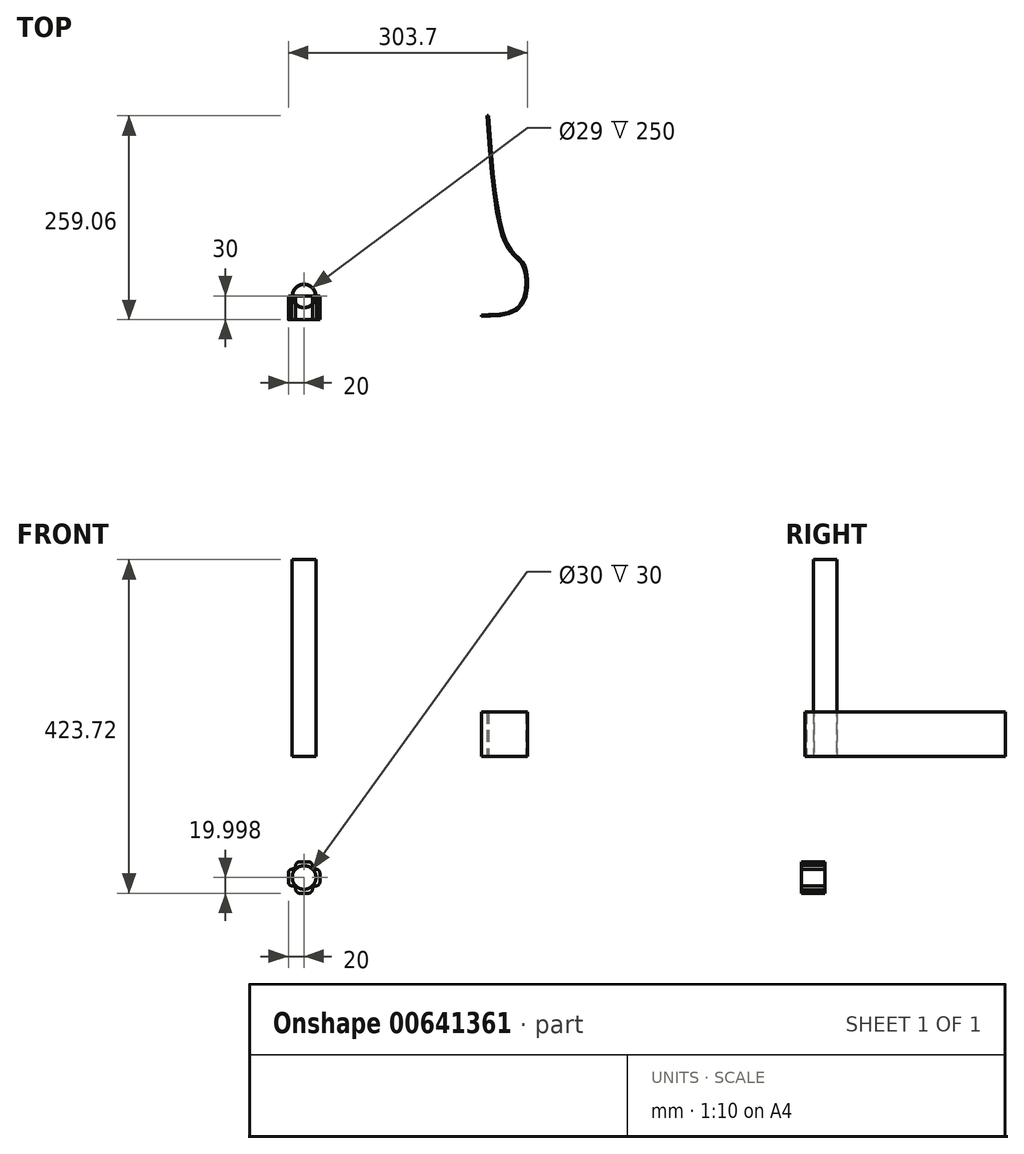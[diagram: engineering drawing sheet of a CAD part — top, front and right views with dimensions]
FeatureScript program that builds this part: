
annotation { "Feature Type Name" : "Feature", "Feature Type Description" : "" }
export const myFeature = defineFeature(function(context is Context, id is Id, definition is map)
    precondition{}
    {
        {
            var Q0;
            Q0=qCreatedBy(makeId("Top.planeOp"),FACE);
            var sketch = newSketch(context, id + "F0", { "sketchPlane" : qUnion([Q0])});
            skCircle(sketch, "E0", {"center": v(0, 0) * mm, "radius": 15 * mm});
            skCircle(sketch, "E1", {"center": v(0, 0) * mm, "radius": 14.5 * mm});
            skSolve(sketch);
        }
        {
            var Q0;
            Q0=qSketchRegion(id+"F0",true);
            extrude(context, id + "F1", {"entities" : qUnion([Q0]), "depth" : 250 * mm});
        }
        {
            var Q0;
            Q0=qCreatedBy(makeId("Front.planeOp"),FACE);
            var sketch = newSketch(context, id + "F2", { "sketchPlane" : qUnion([Q0])});
            skCircle(sketch, "E2", {"center": v(0, -153.72) * mm, "radius": 15 * mm});
            skLineSegment(sketch, "E3.0", {"start": v(-5.6, -133.72) * mm, "end": v(5.6, -133.72) * mm});
            skLineSegment(sketch, "E3.1", {"start": v(20, -148.12) * mm, "end": v(20, -159.33) * mm});
            skLineSegment(sketch, "E3.2", {"start": v(5.6, -173.72) * mm, "end": v(-5.6, -173.72) * mm});
            skLineSegment(sketch, "E3.3", {"start": v(-20, -159.33) * mm, "end": v(-20, -148.12) * mm});
            skPoint(sketch, "E3.0.midPoint", {"position": v(0, -133.72) * mm});
            skPoint(sketch, "E4", {"position": v(20, -153.72) * mm});
            skLineSegment(sketch, "E5", {"start": v(20, -133.72) * mm, "end": v(-20, -173.72) * mm, "construction": true});
            skLineSegment(sketch, "E6", {"start": v(20, -173.72) * mm, "end": v(-20, -133.72) * mm, "construction": true});
            skPoint(sketch, "E7", {"position": v(10.6, -143.12) * mm});
            skPoint(sketch, "E8", {"position": v(-10.6, -164.33) * mm});
            skPoint(sketch, "E9", {"position": v(10.6, -164.33) * mm});
            skPoint(sketch, "E10", {"position": v(-10.6, -143.12) * mm});
            skLineSegment(sketch, "E11.top", {"start": v(15.6, -143.12) * mm, "end": v(15, -143.12) * mm});
            skLineSegment(sketch, "E11.right", {"start": v(10.6, -138.12) * mm, "end": v(10.6, -138.72) * mm});
            skLineSegment(sketch, "E12.top", {"start": v(15.6, -164.33) * mm, "end": v(15, -164.33) * mm});
            skLineSegment(sketch, "E12.right", {"start": v(10.6, -169.33) * mm, "end": v(10.6, -168.72) * mm});
            skLineSegment(sketch, "E13.top", {"start": v(-15.6, -164.33) * mm, "end": v(-15, -164.33) * mm});
            skLineSegment(sketch, "E13.right", {"start": v(-10.6, -169.33) * mm, "end": v(-10.6, -168.72) * mm});
            skLineSegment(sketch, "E14.top", {"start": v(-15.6, -143.12) * mm, "end": v(-15, -143.12) * mm});
            skLineSegment(sketch, "E14.right", {"start": v(-10.6, -138.12) * mm, "end": v(-10.6, -138.72) * mm});
            skArc(sketch, "E15.filletArc", {"start": v(-10.6, -169.33) * mm, "mid": v(-12.07, -165.8) * mm, "end": v(-15.6, -164.33) * mm});
            skArc(sketch, "E16.filletArc", {"start": v(-15.6, -143.12) * mm, "mid": v(-12.07, -141.65) * mm, "end": v(-10.6, -138.12) * mm});
            skArc(sketch, "E17.filletArc", {"start": v(10.6, -138.12) * mm, "mid": v(12.07, -141.65) * mm, "end": v(15.6, -143.12) * mm});
            skArc(sketch, "E18.filletArc", {"start": v(15.6, -164.33) * mm, "mid": v(12.07, -165.8) * mm, "end": v(10.6, -169.33) * mm});
            skPoint(sketch, "E19.visualSharp", {"position": v(20, -164.33) * mm});
            skArc(sketch, "E19.filletArc", {"start": v(15, -164.33) * mm, "mid": v(18.54, -162.86) * mm, "end": v(20, -159.33) * mm});
            skPoint(sketch, "E20.visualSharp", {"position": v(20, -143.12) * mm});
            skArc(sketch, "E20.filletArc", {"start": v(20, -148.12) * mm, "mid": v(18.54, -144.58) * mm, "end": v(15, -143.12) * mm});
            skPoint(sketch, "E21.visualSharp", {"position": v(10.6, -133.72) * mm});
            skArc(sketch, "E21.filletArc", {"start": v(10.6, -138.72) * mm, "mid": v(9.14, -135.19) * mm, "end": v(5.6, -133.72) * mm});
            skPoint(sketch, "E22.visualSharp", {"position": v(-10.6, -133.72) * mm});
            skArc(sketch, "E22.filletArc", {"start": v(-5.6, -133.72) * mm, "mid": v(-9.14, -135.19) * mm, "end": v(-10.6, -138.72) * mm});
            skPoint(sketch, "E23.visualSharp", {"position": v(-20, -143.12) * mm});
            skArc(sketch, "E23.filletArc", {"start": v(-15, -143.12) * mm, "mid": v(-18.54, -144.58) * mm, "end": v(-20, -148.12) * mm});
            skPoint(sketch, "E24.visualSharp", {"position": v(-20, -164.33) * mm});
            skArc(sketch, "E24.filletArc", {"start": v(-20, -159.33) * mm, "mid": v(-18.54, -162.86) * mm, "end": v(-15, -164.33) * mm});
            skPoint(sketch, "E25.visualSharp", {"position": v(-10.6, -173.72) * mm});
            skArc(sketch, "E25.filletArc", {"start": v(-10.6, -168.72) * mm, "mid": v(-9.14, -172.26) * mm, "end": v(-5.6, -173.72) * mm});
            skPoint(sketch, "E26.visualSharp", {"position": v(10.6, -173.72) * mm});
            skArc(sketch, "E26.filletArc", {"start": v(5.6, -173.72) * mm, "mid": v(9.14, -172.26) * mm, "end": v(10.6, -168.72) * mm});
            skSolve(sketch);
        }
        {
            var Q0;
            Q0=qSketchRegion(id+"F2",true);
            extrude(context, id + "F3", {"entities" : qUnion([Q0]), "depth" : 30 * mm});
        }
        {
            var Q0;
            Q0=qCreatedBy(makeId("Top.planeOp"),FACE);
            var sketch = newSketch(context, id + "F4", { "sketchPlane" : qUnion([Q0])});
            skLineSegment(sketch, "E27", {"start": v(195.56, 229.06) * mm, "end": v(195.56, -25.94) * mm, "construction": true});
            skLineSegment(sketch, "E28", {"start": v(225.56, 229.06) * mm, "end": v(225.56, -25.94) * mm});
            skFitSpline(sketch, "E29", {"points": [v(234.4, 229.06) * mm, v(258.34, 65.82) * mm, v(275.52, 45.77) * mm, v(282.68, 29.07) * mm, v(274.56, -14.36) * mm, v(225.56, -25.94) * mm, v(195.56, -25.94) * mm], "startDerivative": vector(48.25, -659.53) * mm, "endDerivative": vector(-199.67, 0.53) * mm});
            skFitSpline(sketch, "E30.0", {"points": [v(232.41, 228.92) * mm, v(233.42, 215.18) * mm, v(235.43, 187.69) * mm, v(238.89, 148.44) * mm, v(242.52, 119.07) * mm, v(246.1, 98.57) * mm, v(248.66, 87.2) * mm, v(250.95, 79.09) * mm, v(252.8, 73.53) * mm, v(254.45, 69.35) * mm, v(255.85, 66.29) * mm, v(257.3, 63.42) * mm, v(259.22, 60.23) * mm, v(262.4, 55.84) * mm, v(265.63, 52.37) * mm, v(268.7, 49.5) * mm, v(270.85, 47.55) * mm, v(272.47, 46.05) * mm, v(273.63, 44.87) * mm, v(274.7, 43.7) * mm, v(275.9, 42.2) * mm, v(277.54, 39.67) * mm, v(278.84, 36.73) * mm, v(279.87, 33.11) * mm, v(280.42, 30.5) * mm, v(280.8, 28.19) * mm, v(281.14, 25.71) * mm, v(281.48, 22.38) * mm, v(281.71, 18.09) * mm, v(281.7, 12.12) * mm, v(281.16, 5.99) * mm, v(279.92, 0.12) * mm, v(278.6, -4.05) * mm, v(276.87, -7.88) * mm, v(275.06, -10.72) * mm, v(273.38, -12.74) * mm, v(271.54, -14.57) * mm, v(268.9, -16.59) * mm, v(265.24, -18.59) * mm, v(259.81, -20.74) * mm, v(252.19, -22.53) * mm, v(244, -23.42) * mm, v(237.46, -23.76) * mm, v(232.63, -23.89) * mm, v(228.74, -23.93) * mm, v(225.75, -23.94) * mm, v(222.85, -23.95) * mm, v(219.41, -23.96) * mm, v(214.25, -23.97) * mm, v(208.33, -23.97) * mm, v(201.8, -23.96) * mm, v(197.65, -23.94) * mm, v(195.57, -23.94) * mm]});
            skLineSegment(sketch, "E31", {"start": v(232.41, 228.92) * mm, "end": v(234.4, 229.06) * mm});
            skSolve(sketch);
        }
        {
            var Q0;
            Q0=qSketchRegion(id+"F4",true);
            extrude(context, id + "F5", {"entities" : qUnion([Q0]), "depth" : 56.47 * mm});
        }
    });
